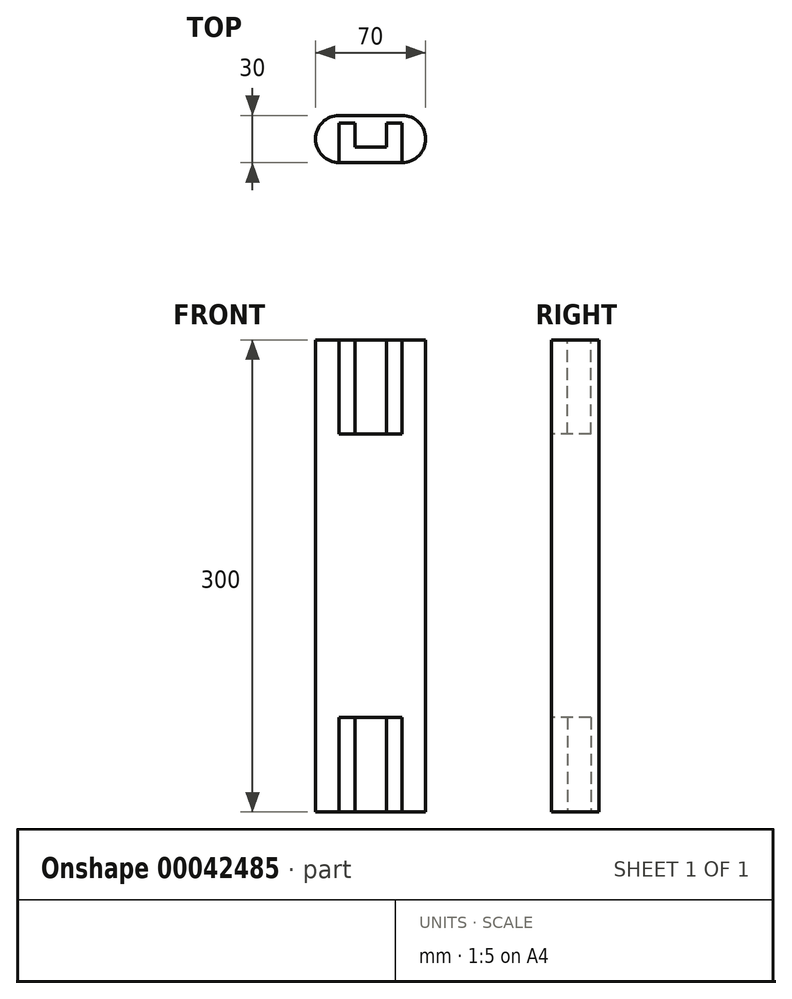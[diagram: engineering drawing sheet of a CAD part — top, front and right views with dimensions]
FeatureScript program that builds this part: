
annotation { "Feature Type Name" : "Feature", "Feature Type Description" : "" }
export const myFeature = defineFeature(function(context is Context, id is Id, definition is map)
    precondition{}
    {
        {
            var Q0;
            Q0=qCreatedBy(makeId("Top.planeOp"),FACE);
            var sketch = newSketch(context, id + "F0", { "sketchPlane" : qUnion([Q0])});
            skLineSegment(sketch, "E0", {"start": v(0, -27.55) * mm, "end": v(0, 32.32) * mm, "construction": true});
            skLineSegment(sketch, "E1", {"start": v(-29.9, 0) * mm, "end": v(37.28, 0) * mm, "construction": true});
            skLineSegment(sketch, "E2.bottom", {"start": v(0, 15) * mm, "end": v(-20, 15) * mm});
            skLineSegment(sketch, "E2.top", {"start": v(0, -15) * mm, "end": v(-20, -15) * mm});
            skArc(sketch, "E3", {"start": v(-20, 15) * mm, "mid": v(-35, 0) * mm, "end": v(-20, -15) * mm});
            skPoint(sketch, "E3.centerSnap0", {"position": v(-20, 0) * mm});
            skLineSegment(sketch, "E4.MirrorCS", {"start": v(0, 15) * mm, "end": v(20, 15) * mm});
            skArc(sketch, "E5.MirrorCS", {"start": v(20, 15) * mm, "mid": v(35, 0) * mm, "end": v(20, -15) * mm});
            skLineSegment(sketch, "E6.MirrorCS", {"start": v(0, -15) * mm, "end": v(20, -15) * mm});
            skSolve(sketch);
        }
        {
            var Q0;
            Q0 = qSketchRegion(id + "F0", true);
            extrude(context, id + "F1", {"entities" : qUnion([Q0]), "depth" : 300 * mm});
        }
        {
            var Q0;
            Q0=makeQuery(id+"F1.opExtrude","CAP_FACE",FACE,{"disambiguationData":[OSD([sQuery(id+"F0.wireOp",EDGE,"E2.bottom"),sQuery(id+"F0.wireOp",EDGE,"E2.top"),sQuery(id+"F0.wireOp",EDGE,"E3"),sQuery(id+"F0.wireOp",EDGE,"E4.MirrorCS"),sQuery(id+"F0.wireOp",EDGE,"E5.MirrorCS"),sQuery(id+"F0.wireOp",EDGE,"E6.MirrorCS")])],"isStart":false});
            var sketch = newSketch(context, id + "F2", { "sketchPlane" : qUnion([Q0])});
            skLineSegment(sketch, "E7", {"start": v(0, 37.44) * mm, "end": v(0, -31.74) * mm, "construction": true});
            skLineSegment(sketch, "E8", {"start": v(-56.01, 0) * mm, "end": v(59.19, 0) * mm, "construction": true});
            skLineSegment(sketch, "E9", {"start": v(-20, 10) * mm, "end": v(-10, 10) * mm});
            skLineSegment(sketch, "E10", {"start": v(-20, 10) * mm, "end": v(-20, -18.43) * mm});
            skLineSegment(sketch, "E11", {"start": v(-10, 10) * mm, "end": v(-10, -5) * mm});
            skLineSegment(sketch, "E12", {"start": v(-10, -5) * mm, "end": v(0, -5) * mm});
            skLineSegment(sketch, "E13", {"start": v(-20, -18.43) * mm, "end": v(0, -18.43) * mm});
            skLineSegment(sketch, "E14.MirrorCS", {"start": v(20, -18.43) * mm, "end": v(0, -18.43) * mm});
            skLineSegment(sketch, "E15.MirrorCS", {"start": v(20, 10) * mm, "end": v(20, -18.43) * mm});
            skLineSegment(sketch, "E16.MirrorCS", {"start": v(20, 10) * mm, "end": v(10, 10) * mm});
            skLineSegment(sketch, "E17.MirrorCS", {"start": v(10, 10) * mm, "end": v(10, -5) * mm});
            skLineSegment(sketch, "E18.MirrorCS", {"start": v(10, -5) * mm, "end": v(0, -5) * mm});
            skPoint(sketch, "E19.orphan", {"position": v(-51.9, 10) * mm});
            skPoint(sketch, "E20.orphan", {"position": v(51.9, 10) * mm});
            skSolve(sketch);
        }
        {
            var Q0;
            Q0 = qSketchRegion(id + "F2", true);
            extrude(context, id + "F3", {"entities" : qUnion([Q0]), "operationType" : NewBodyOperationType.REMOVE, "oppositeDirection" : true, "depth" : 60 * mm});
        }
        {
            var Q0;
            Q0=makeQuery(id+"F1.opExtrude","CAP_FACE",FACE,{"disambiguationData":[OSD([sQuery(id+"F0.wireOp",EDGE,"E2.bottom"),sQuery(id+"F0.wireOp",EDGE,"E2.top"),sQuery(id+"F0.wireOp",EDGE,"E3"),sQuery(id+"F0.wireOp",EDGE,"E4.MirrorCS"),sQuery(id+"F0.wireOp",EDGE,"E5.MirrorCS"),sQuery(id+"F0.wireOp",EDGE,"E6.MirrorCS")])],"isStart":true});
            var sketch = newSketch(context, id + "F4", { "sketchPlane" : qUnion([Q0])});
            skLineSegment(sketch, "E21", {"start": v(0, -44.14) * mm, "end": v(0, 51) * mm, "construction": true});
            skLineSegment(sketch, "E22", {"start": v(64.43, 0) * mm, "end": v(-61.48, 0) * mm, "construction": true});
            skLineSegment(sketch, "E23", {"start": v(20, -10) * mm, "end": v(10, -10) * mm});
            skLineSegment(sketch, "E24", {"start": v(20, -10) * mm, "end": v(20, 20.5) * mm});
            skLineSegment(sketch, "E25", {"start": v(10, -10) * mm, "end": v(10, 5) * mm});
            skLineSegment(sketch, "E26", {"start": v(10, 5) * mm, "end": v(0, 5) * mm});
            skLineSegment(sketch, "E27", {"start": v(20, 20.5) * mm, "end": v(0, 20.5) * mm});
            skLineSegment(sketch, "E28.MirrorCS", {"start": v(-20, 20.5) * mm, "end": v(0, 20.5) * mm});
            skLineSegment(sketch, "E29.MirrorCS", {"start": v(-20, -10) * mm, "end": v(-20, 20.5) * mm});
            skLineSegment(sketch, "E30.MirrorCS", {"start": v(-20, -10) * mm, "end": v(-10, -10) * mm});
            skLineSegment(sketch, "E31.MirrorCS", {"start": v(-10, 5) * mm, "end": v(0, 5) * mm});
            skLineSegment(sketch, "E32.MirrorCS", {"start": v(-10, -10) * mm, "end": v(-10, 5) * mm});
            skSolve(sketch);
        }
        {
            var Q0;
            Q0 = qSketchRegion(id + "F4", true);
            extrude(context, id + "F5", {"entities" : qUnion([Q0]), "operationType" : NewBodyOperationType.REMOVE, "oppositeDirection" : true, "depth" : 60 * mm});
        }
    });
